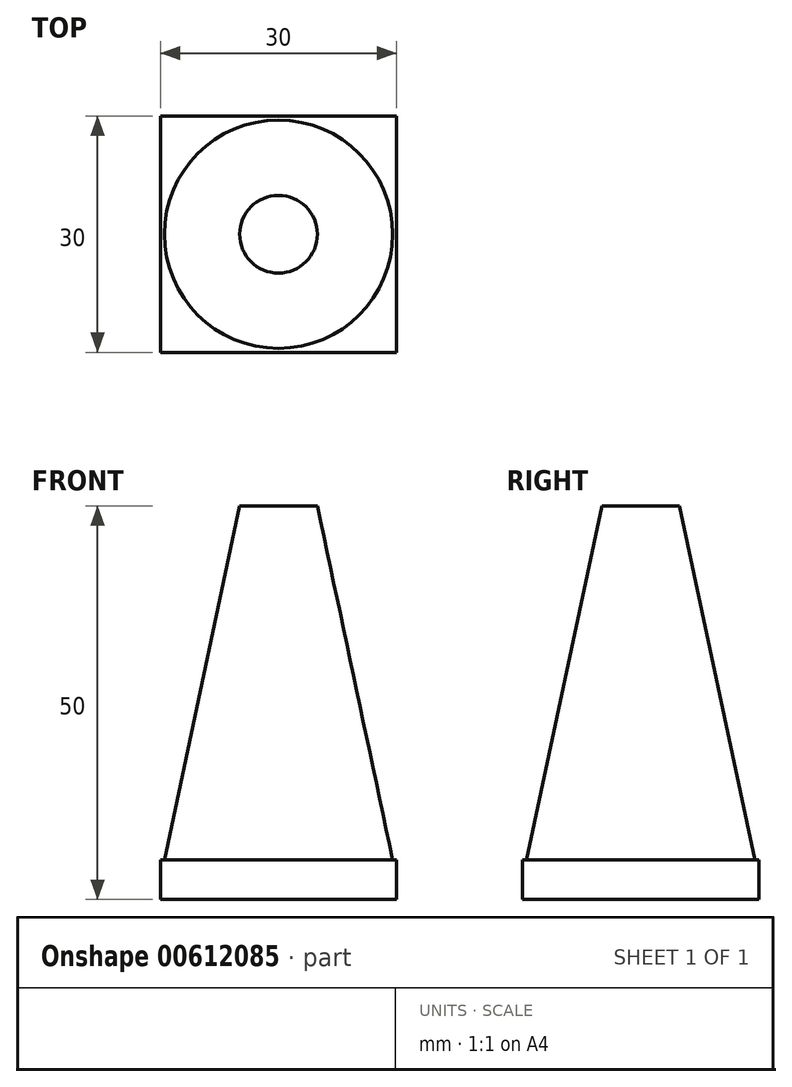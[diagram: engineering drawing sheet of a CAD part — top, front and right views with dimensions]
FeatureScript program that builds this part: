
annotation { "Feature Type Name" : "Feature", "Feature Type Description" : "" }
export const myFeature = defineFeature(function(context is Context, id is Id, definition is map)
    precondition{}
    {
        {
            var Q0;
            Q0=qCreatedBy(makeId("Top.planeOp"),FACE);
            var sketch = newSketch(context, id + "F0", { "sketchPlane" : qUnion([Q0])});
            skSolve(sketch);
        }
        {
            var Q0;
            Q0=qCreatedBy(makeId("Front.planeOp"),FACE);
            var sketch = newSketch(context, id + "F1", { "sketchPlane" : qUnion([Q0])});
            skLineSegment(sketch, "E0.bottom", {"start": v(-15, 2.5) * mm, "end": v(15, 2.5) * mm});
            skLineSegment(sketch, "E0.top", {"start": v(-15, -2.5) * mm, "end": v(15, -2.5) * mm});
            skLineSegment(sketch, "E0.left", {"start": v(-15, 2.5) * mm, "end": v(-15, -2.5) * mm});
            skLineSegment(sketch, "E0.right", {"start": v(15, 2.5) * mm, "end": v(15, -2.5) * mm});
            skPoint(sketch, "E0.middle", {"position": v(0, 0) * mm});
            skLineSegment(sketch, "E1", {"start": v(0, 2.5) * mm, "end": v(0, 47.5) * mm});
            skPoint(sketch, "E1.endSnap0", {"position": v(0, 2.5) * mm});
            skLineSegment(sketch, "E2.bottom", {"start": v(12.5, 2.5) * mm, "end": v(-12.5, 2.5) * mm});
            skLineSegment(sketch, "E2.top", {"start": v(12.5, 47.5) * mm, "end": v(-12.5, 47.5) * mm});
            skLineSegment(sketch, "E2.left", {"start": v(12.5, 2.5) * mm, "end": v(12.5, 47.5) * mm});
            skLineSegment(sketch, "E2.right", {"start": v(-12.5, 2.5) * mm, "end": v(-12.5, 47.5) * mm});
            skPoint(sketch, "E2.middle", {"position": v(0, 25) * mm});
            skSolve(sketch);
        }
        {
            var Q0;
            Q0=makeQuery(id+"F1.imprint","IMPRINT",FACE,{"disambiguationData":[TD([[makeQuery(id+"F1.imprint","IMPRINT",EDGE,{"derivedFrom":sQuery(id+"F1.wireOp",EDGE,"E0.top")}),1.0]])]});
            extrude(context, id + "F2", {"entities" : qUnion([Q0]), "endBound" : BoundingType.SYMMETRIC, "depth" : 30 * mm, "offsetDistance" : 25 * mm});
        }
        {
            var Q0;
            Q0=makeQuery(id+"F2.opExtrude","SWEPT_FACE",FACE,{"disambiguationData":[OSD([sQuery(id+"F1.wireOp",EDGE,"E0.bottom"),sQuery(id+"F1.wireOp",EDGE,"E2.bottom")])]});
            var sketch = newSketch(context, id + "F3", { "sketchPlane" : qUnion([Q0])});
            skCircle(sketch, "E3", {"center": v(0, 0) * mm, "radius": 14.5 * mm});
            skSolve(sketch);
        }
        {
            var Q0;
            Q0=makeQuery(id+"F3.imprint","IMPRINT",FACE,{"disambiguationData":[TD([[makeQuery(id+"F3.imprint","IMPRINT",EDGE,{"derivedFrom":sQuery(id+"F3.wireOp",EDGE,"E3")}),1.0]])]});
            extrude(context, id + "F4", {"entities" : qUnion([Q0]), "operationType" : NewBodyOperationType.ADD, "depth" : 45 * mm, "offsetDistance" : 25 * mm, "hasDraft" : true, "draftAngle" : 12 * degree, "draftPullDirection" : true});
        }
    });
